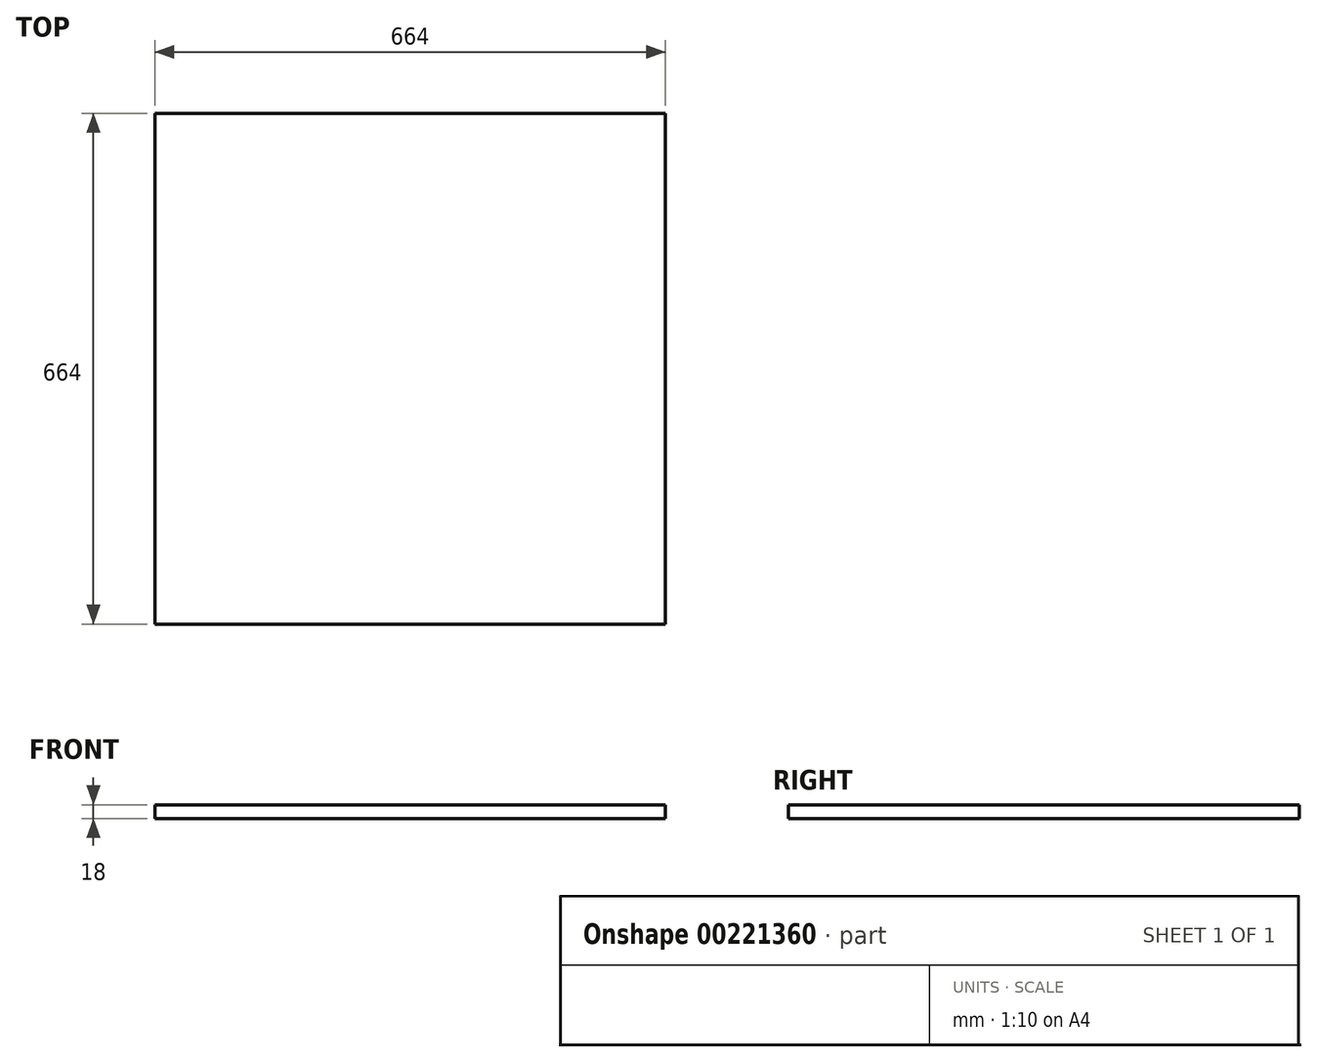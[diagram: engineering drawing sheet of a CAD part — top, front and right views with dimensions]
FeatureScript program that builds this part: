
annotation { "Feature Type Name" : "Feature", "Feature Type Description" : "" }
export const myFeature = defineFeature(function(context is Context, id is Id, definition is map)
    precondition{}
    {
        {
            var Q0;
            Q0=qCreatedBy(makeId("Top.planeOp"),FACE);
            var sketch = newSketch(context, id + "F0", { "sketchPlane" : qUnion([Q0])});
            skLineSegment(sketch, "E0.bottom", {"start": v(332, -332) * mm, "end": v(-332, -332) * mm});
            skLineSegment(sketch, "E0.top", {"start": v(332, 332) * mm, "end": v(-332, 332) * mm});
            skLineSegment(sketch, "E0.left", {"start": v(332, -332) * mm, "end": v(332, 332) * mm});
            skLineSegment(sketch, "E0.right", {"start": v(-332, -332) * mm, "end": v(-332, 332) * mm});
            skPoint(sketch, "E0.middle", {"position": v(0, 0) * mm});
            skSolve(sketch);
        }
        {
            var Q0;
            Q0 = qSketchRegion(id + "F0", true);
            extrude(context, id + "F1", {"entities" : qUnion([Q0]), "depth" : 18 * mm});
        }
    });
